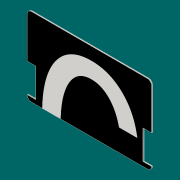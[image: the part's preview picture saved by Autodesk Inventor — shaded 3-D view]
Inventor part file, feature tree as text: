
AUTODESK INVENTOR PART (.ipt)
format: ipt  version: 2016 (Build 200138000, 138)  size: 219,136 bytes
history: native  units: mm
features: sketch x5, extrude x3, projected_geometry x3, other x2, fillet x1, mirror x1
ambient origin geometry x8: Origin, YZ Plane, XZ Plane, XY Plane, X Axis, Y Axis, Z Axis, Center Point
bodies: Solid1 (feature_tree)
feature tree (15):
  extrude  "Extrusion1"  Depth=53.98mm
  fillet  "Fillet1"  Radius=0.76mm
  extrude  "Extrusion2"  Depth=2.88mm
  extrude  "Extrusion3"  Depth=5.588mm
  mirror  "Mirror1"
  other  "Decal1"
  other  "Decal2"
  sketch  "Sketch1"  dims[d0=85.6mm d1=53.98mm d2=0.76mm]
  sketch  "Sketch2"  dims[d3=0.0mm d4=2.88mm]
  projected_geometry  "Projected Loop1"
  sketch  "Sketch3"  dims[d5=5.588mm d6=5.588mm]
  sketch  "Sketch4"  dims[d7=3.0mm]
  projected_geometry  "Projected Loop2"
  sketch  "Sketch5"  dims[d8=3.0mm d9=20.0mm d10=20.0mm d11=0.76mm d12=0.0mm d13=3.0mm d14=3.0mm d15=0.76mm d16=1.5mm d17=1.5mm d18=1.5mm d19=0.76mm d20=0.0mm]
  projected_geometry  "Projected Loop3"
